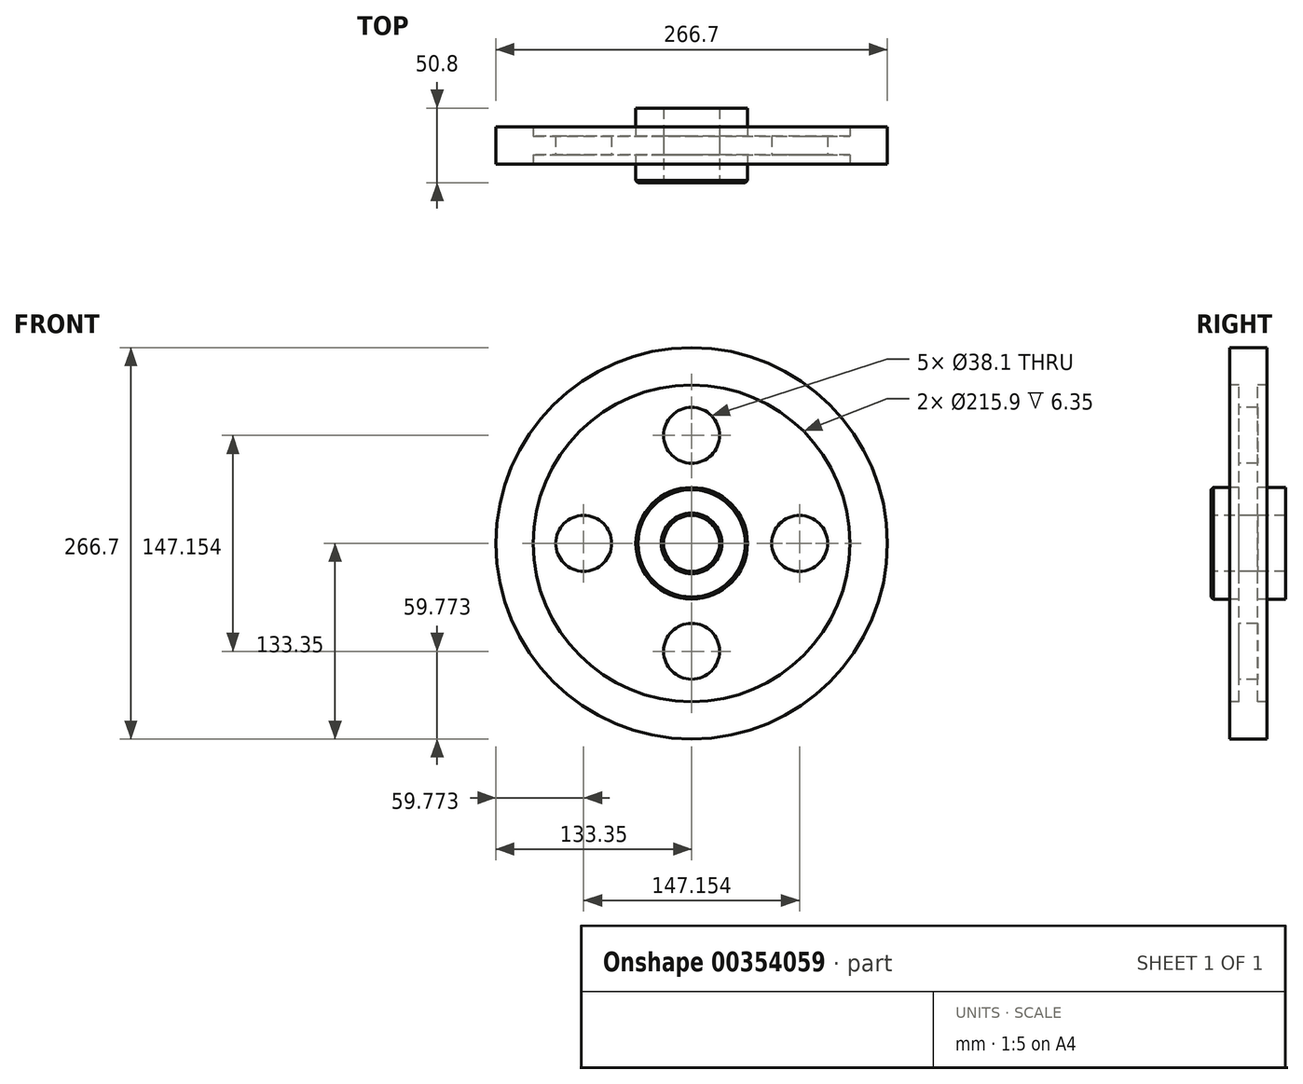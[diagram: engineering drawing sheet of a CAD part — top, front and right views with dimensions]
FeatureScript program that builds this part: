
annotation { "Feature Type Name" : "Feature", "Feature Type Description" : "" }
export const myFeature = defineFeature(function(context is Context, id is Id, definition is map)
    precondition{}
    {
        {
            var Q0;
            Q0=qCreatedBy(makeId("Right.planeOp"),FACE);
            var sketch = newSketch(context, id + "F0", { "sketchPlane" : qUnion([Q0])});
            skLineSegment(sketch, "E0", {"start": v(0, 0) * mm, "end": v(76.28, 0) * mm, "construction": true});
            skLineSegment(sketch, "E1.0", {"start": v(0, 19.05) * mm, "end": v(25.4, 19.05) * mm});
            skLineSegment(sketch, "E2.0", {"start": v(6.35, 38.1) * mm, "end": v(25.4, 38.1) * mm});
            skLineSegment(sketch, "E3.0", {"start": v(0, 133.35) * mm, "end": v(12.7, 133.35) * mm});
            skLineSegment(sketch, "E4", {"start": v(0, 133.35) * mm, "end": v(0, 38.1) * mm, "construction": true});
            skLineSegment(sketch, "E5.0", {"start": v(25.4, 38.1) * mm, "end": v(25.4, 19.05) * mm});
            skLineSegment(sketch, "E6.0", {"start": v(12.7, 133.35) * mm, "end": v(12.7, 107.95) * mm});
            skLineSegment(sketch, "E7.trimOffspring", {"start": v(0, 38.1) * mm, "end": v(0, 0) * mm, "construction": true});
            skLineSegment(sketch, "E8", {"start": v(6.35, 107.95) * mm, "end": v(12.7, 107.95) * mm});
            skLineSegment(sketch, "E9", {"start": v(6.35, 107.95) * mm, "end": v(6.35, 38.1) * mm});
            skPoint(sketch, "E10.orphan", {"position": v(0, 107.95) * mm});
            skLineSegment(sketch, "E11.MirrorCS", {"start": v(-6.35, 107.95) * mm, "end": v(-6.35, 38.1) * mm});
            skLineSegment(sketch, "E12.MirrorCS", {"start": v(-12.7, 133.35) * mm, "end": v(-12.7, 107.95) * mm});
            skLineSegment(sketch, "E13.MirrorCS", {"start": v(-6.35, 107.95) * mm, "end": v(-12.7, 107.95) * mm});
            skLineSegment(sketch, "E14.MirrorCS", {"start": v(0, 133.35) * mm, "end": v(-12.7, 133.35) * mm});
            skLineSegment(sketch, "E15.MirrorCS", {"start": v(-6.35, 38.1) * mm, "end": v(-25.4, 38.1) * mm});
            skLineSegment(sketch, "E16.MirrorCS", {"start": v(0, 19.05) * mm, "end": v(-25.4, 19.05) * mm});
            skLineSegment(sketch, "E17.MirrorCS", {"start": v(-25.4, 38.1) * mm, "end": v(-25.4, 19.05) * mm});
            skSolve(sketch);
        }
        {
            var Q0;
            Q0 = qSketchRegion(id + "F0", true);
            var Q1;
            Q1=sQuery(id+"F0.wireOp",EDGE,"E0");
            revolve(context, id + "F1", {"entities" : qUnion([Q0]), "axis" : qUnion([Q1]), "revolveType" : RevolveType.FULL});
        }
        {
            var Q0;
            Q0=makeQuery(id+"F1.opRevolve","SWEPT_FACE",FACE,{"disambiguationData":[OSD([sQuery(id+"F0.wireOp",EDGE,"E11.MirrorCS")])]});
            var sketch = newSketch(context, id + "F2", { "sketchPlane" : qUnion([Q0])});
            skLineSegment(sketch, "E18", {"start": v(0, 0) * mm, "end": v(0, 45.03) * mm});
            skLineSegment(sketch, "E19", {"start": v(0, 0) * mm, "end": v(0, 73.58) * mm});
            skCircle(sketch, "E20", {"center": v(0, 73.58) * mm, "radius": 19.05 * mm});
            skLineSegment(sketch, "E21.direction1", {"start": v(0, 73.58) * mm, "end": v(25.4, 73.58) * mm, "construction": true});
            skCircle(sketch, "E22.1.0", {"center": v(-73.58, 0) * mm, "radius": 19.05 * mm});
            skCircle(sketch, "E22.2.0", {"center": v(0, -73.58) * mm, "radius": 19.05 * mm});
            skPoint(sketch, "E22.center", {"position": v(0, 0) * mm});
            skCircle(sketch, "E23.1.3.0", {"center": v(73.58, 0) * mm, "radius": 19.05 * mm});
            skSolve(sketch);
        }
        {
            var Q0;
            Q0=makeQuery(id+"F2.imprint","IMPRINT",FACE,{"disambiguationData":[TD([[makeQuery(id+"F2.imprint","IMPRINT",EDGE,{"derivedFrom":sQuery(id+"F2.wireOp",EDGE,"E23.1.3.0")}),1.0]])]});
            var Q1;
            Q1=makeQuery(id+"F2.imprint","IMPRINT",FACE,{"disambiguationData":[TD([[makeQuery(id+"F2.imprint","IMPRINT",EDGE,{"derivedFrom":sQuery(id+"F2.wireOp",EDGE,"E22.2.0")}),1.0]])]});
            var Q2;
            Q2=makeQuery(id+"F2.imprint","IMPRINT",FACE,{"disambiguationData":[TD([[makeQuery(id+"F2.imprint","IMPRINT",EDGE,{"derivedFrom":sQuery(id+"F2.wireOp",EDGE,"E22.1.0")}),1.0]])]});
            var Q3;
            Q3=makeQuery(id+"F2.imprint","IMPRINT",FACE,{"disambiguationData":[TD([[makeQuery(id+"F2.imprint","IMPRINT",EDGE,{"derivedFrom":sQuery(id+"F2.wireOp",EDGE,"E20")}),1.0]])]});
            extrude(context, id + "F3", {"entities" : qUnion([Q0, Q1, Q2, Q3]), "operationType" : NewBodyOperationType.REMOVE, "oppositeDirection" : true, "depth" : 25.4 * mm});
        }
        {
            var Q0;
            Q0=makeQuery(id+"F1.opRevolve","SWEPT_EDGE",EDGE,{"disambiguationData":[OSD([sQuery(id+"F0.wireOp",EDGE,"E16.MirrorCS"),sQuery(id+"F0.wireOp",EDGE,"E17.MirrorCS")])]});
            var Q1;
            Q1=makeQuery(id+"F1.opRevolve","SWEPT_EDGE",EDGE,{"disambiguationData":[OSD([sQuery(id+"F0.wireOp",EDGE,"E15.MirrorCS"),sQuery(id+"F0.wireOp",EDGE,"E17.MirrorCS")])]});
            chamfer(context, id + "F4", {"entities" : qUnion([Q0, Q1]), "width" : 1.59 * mm, "tangentPropagation" : true});
        }
    });
